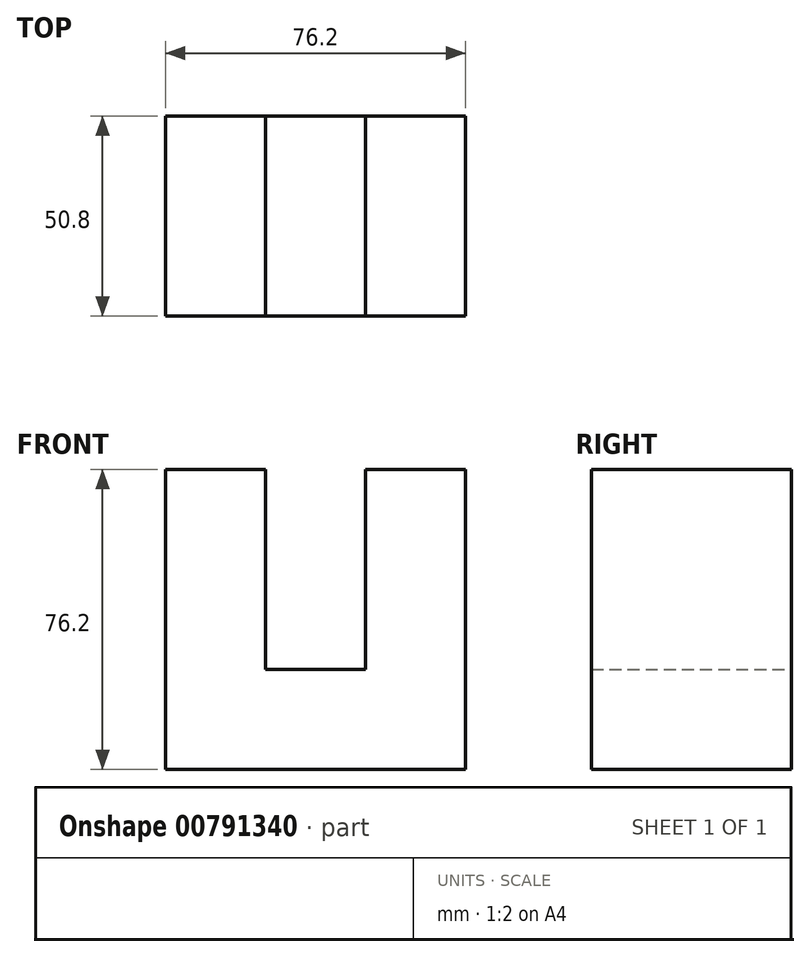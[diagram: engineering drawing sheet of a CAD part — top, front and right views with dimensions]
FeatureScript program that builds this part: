
annotation { "Feature Type Name" : "Feature", "Feature Type Description" : "" }
export const myFeature = defineFeature(function(context is Context, id is Id, definition is map)
    precondition{}
    {
        {
            var Q0;
            Q0=qCreatedBy(makeId("Front.planeOp"),FACE);
            var sketch = newSketch(context, id + "F0", { "sketchPlane" : qUnion([Q0])});
            skLineSegment(sketch, "E0", {"start": v(0, 76.2) * mm, "end": v(0, 0) * mm});
            skLineSegment(sketch, "E1", {"start": v(0, 0) * mm, "end": v(76.2, 0) * mm});
            skLineSegment(sketch, "E2", {"start": v(76.2, 0) * mm, "end": v(76.2, 76.2) * mm});
            skLineSegment(sketch, "E3", {"start": v(76.2, 76.2) * mm, "end": v(50.8, 76.2) * mm});
            skLineSegment(sketch, "E4", {"start": v(50.8, 76.2) * mm, "end": v(50.8, 25.4) * mm});
            skLineSegment(sketch, "E5", {"start": v(50.8, 25.4) * mm, "end": v(25.4, 25.4) * mm});
            skLineSegment(sketch, "E6", {"start": v(25.4, 25.4) * mm, "end": v(25.4, 76.2) * mm});
            skLineSegment(sketch, "E7", {"start": v(25.4, 76.2) * mm, "end": v(0, 76.2) * mm});
            skSolve(sketch);
        }
        {
            var Q0;
            Q0=qSketchRegion(id+"F0",true);
            extrude(context, id + "F1", {"entities" : qUnion([Q0]), "depth" : 50.8 * mm, "offsetDistance" : 25.4 * mm});
        }
    });
